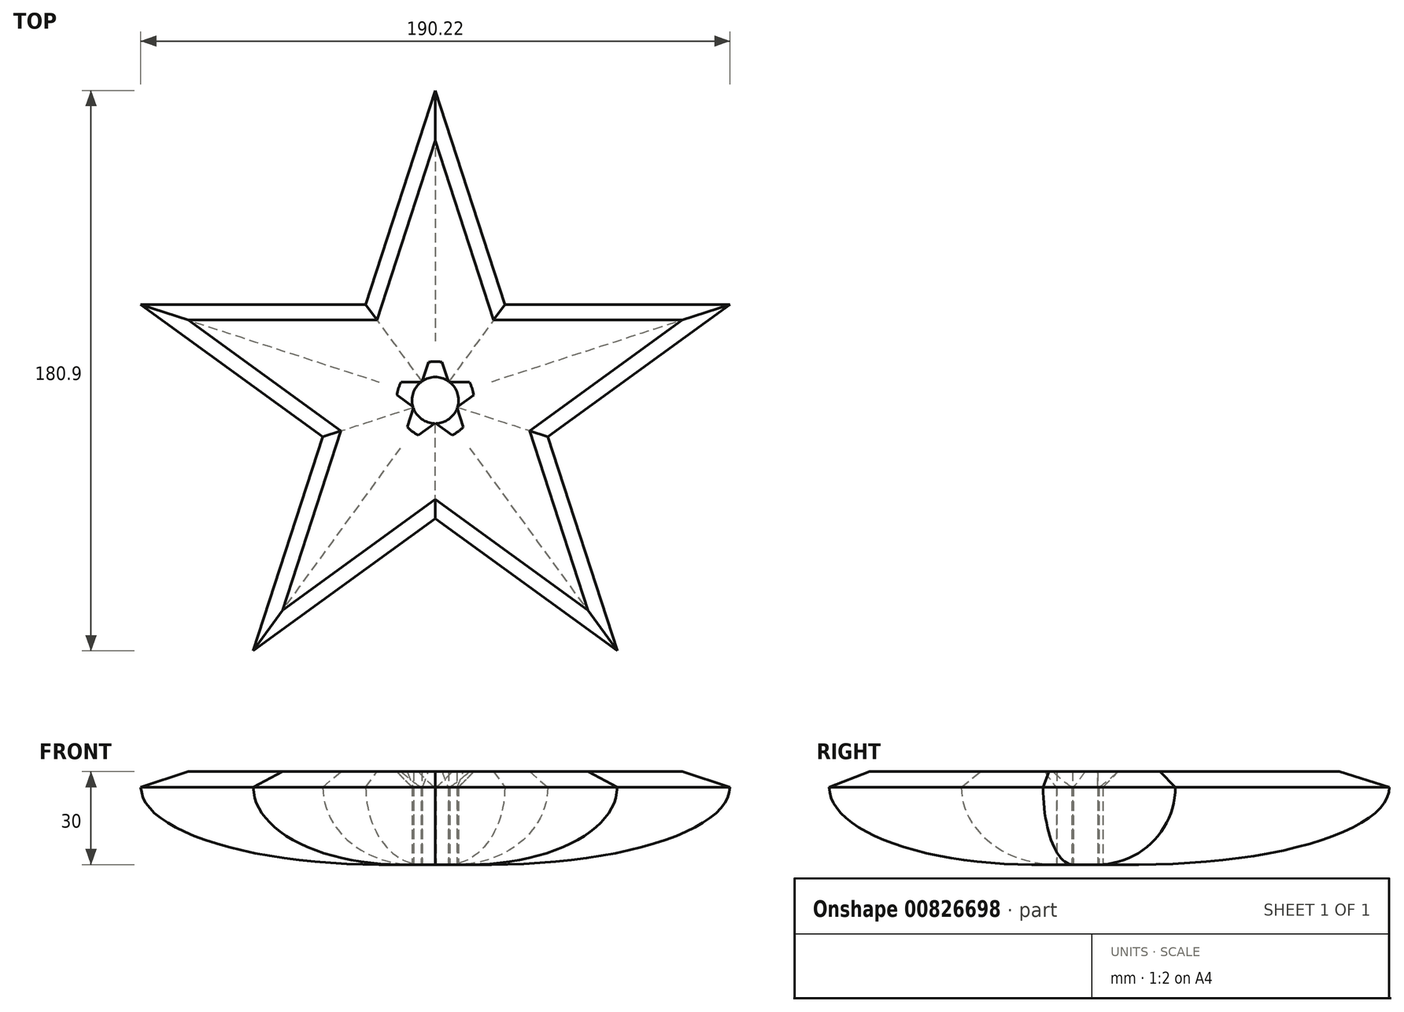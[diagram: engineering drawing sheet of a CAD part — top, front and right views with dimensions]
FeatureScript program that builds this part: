
annotation { "Feature Type Name" : "Feature", "Feature Type Description" : "" }
export const myFeature = defineFeature(function(context is Context, id is Id, definition is map)
    precondition{}
    {
        {
            var Q0;
            Q0=qCreatedBy(makeId("Top.planeOp"),FACE);
            var sketch = newSketch(context, id + "F0", { "sketchPlane" : qUnion([Q0])});
            skCircle(sketch, "E0.cCircle", {"center": v(0, 0) * mm, "radius": 100 * mm, "construction": true});
            skLineSegment(sketch, "E0.0", {"start": v(0, 100) * mm, "end": v(95.1, 30.9) * mm});
            skLineSegment(sketch, "E0.1", {"start": v(95.1, 30.9) * mm, "end": v(58.78, -80.9) * mm});
            skLineSegment(sketch, "E0.2", {"start": v(58.78, -80.9) * mm, "end": v(-58.78, -80.9) * mm});
            skLineSegment(sketch, "E0.3", {"start": v(-58.78, -80.9) * mm, "end": v(-95.1, 30.9) * mm});
            skLineSegment(sketch, "E0.4", {"start": v(-95.1, 30.9) * mm, "end": v(0, 100) * mm});
            skLineSegment(sketch, "E1", {"start": v(0, 100) * mm, "end": v(-22.45, 30.9) * mm});
            skLineSegment(sketch, "E2", {"start": v(95.1, 30.9) * mm, "end": v(22.45, 30.9) * mm});
            skLineSegment(sketch, "E3", {"start": v(-95.1, 30.9) * mm, "end": v(-36.33, -11.8) * mm});
            skLineSegment(sketch, "E4", {"start": v(0, 100) * mm, "end": v(22.45, 30.9) * mm});
            skLineSegment(sketch, "E5", {"start": v(-58.78, -80.9) * mm, "end": v(0, -38.2) * mm});
            skLineSegment(sketch, "E6.trimOffspring", {"start": v(-36.33, -11.8) * mm, "end": v(-58.78, -80.9) * mm});
            skLineSegment(sketch, "E7.trimOffspring", {"start": v(36.33, -11.8) * mm, "end": v(58.78, -80.9) * mm});
            skLineSegment(sketch, "E8.trimOffspring", {"start": v(-22.45, 30.9) * mm, "end": v(-95.1, 30.9) * mm});
            skLineSegment(sketch, "E9.trimOffspring", {"start": v(0, -38.2) * mm, "end": v(58.78, -80.9) * mm});
            skLineSegment(sketch, "E10.trimOffspring", {"start": v(36.33, -11.8) * mm, "end": v(95.1, 30.9) * mm});
            skSolve(sketch);
        }
        {
            var Q0;
            Q0=makeQuery(id+"F0.imprint","IMPRINT",FACE,{"disambiguationData":[TD([[makeQuery(id+"F0.imprint","IMPRINT",EDGE,{"derivedFrom":sQuery(id+"F0.wireOp",EDGE,"E1")}),1.0]])]});
            extrude(context, id + "F1", {"entities" : qUnion([Q0]), "depth" : 30 * mm, "offsetDistance" : 25 * mm});
        }
        {
            var Q0;
            Q0=makeQuery(id+"F1.opExtrude","CAP_FACE",FACE,{"disambiguationData":[OSD([sQuery(id+"F0.wireOp",EDGE,"E1"),sQuery(id+"F0.wireOp",EDGE,"E2"),sQuery(id+"F0.wireOp",EDGE,"E3"),sQuery(id+"F0.wireOp",EDGE,"E4"),sQuery(id+"F0.wireOp",EDGE,"E5"),sQuery(id+"F0.wireOp",EDGE,"E6.trimOffspring"),sQuery(id+"F0.wireOp",EDGE,"E7.trimOffspring"),sQuery(id+"F0.wireOp",EDGE,"E8.trimOffspring"),sQuery(id+"F0.wireOp",EDGE,"E9.trimOffspring"),sQuery(id+"F0.wireOp",EDGE,"E10.trimOffspring")])],"isStart":false});
            chamfer(context, id + "F2", {"entities" : qUnion([Q0]), "width" : 5 * mm, "tangentPropagation" : true});
        }
        {
            var Q0;
            Q0=makeQuery(id+"F1.opExtrude","CAP_FACE",FACE,{"disambiguationData":[OSD([sQuery(id+"F0.wireOp",EDGE,"E1"),sQuery(id+"F0.wireOp",EDGE,"E2"),sQuery(id+"F0.wireOp",EDGE,"E3"),sQuery(id+"F0.wireOp",EDGE,"E4"),sQuery(id+"F0.wireOp",EDGE,"E5"),sQuery(id+"F0.wireOp",EDGE,"E6.trimOffspring"),sQuery(id+"F0.wireOp",EDGE,"E7.trimOffspring"),sQuery(id+"F0.wireOp",EDGE,"E8.trimOffspring"),sQuery(id+"F0.wireOp",EDGE,"E9.trimOffspring"),sQuery(id+"F0.wireOp",EDGE,"E10.trimOffspring")])],"isStart":true});
            fillet(context, id + "F3", {"entities" : qUnion([Q0]), "radius" : 25 * mm, "tangentPropagation" : true, "allowEdgeOverflow" : false});
        }
        {
            var Q0;
            Q0=makeQuery(id+"F1.opExtrude","CAP_FACE",FACE,{"disambiguationData":[OSD([sQuery(id+"F0.wireOp",EDGE,"E1"),sQuery(id+"F0.wireOp",EDGE,"E2"),sQuery(id+"F0.wireOp",EDGE,"E3"),sQuery(id+"F0.wireOp",EDGE,"E4"),sQuery(id+"F0.wireOp",EDGE,"E5"),sQuery(id+"F0.wireOp",EDGE,"E6.trimOffspring"),sQuery(id+"F0.wireOp",EDGE,"E7.trimOffspring"),sQuery(id+"F0.wireOp",EDGE,"E8.trimOffspring"),sQuery(id+"F0.wireOp",EDGE,"E9.trimOffspring"),sQuery(id+"F0.wireOp",EDGE,"E10.trimOffspring")])],"isStart":true});
            var sketch = newSketch(context, id + "F4", { "sketchPlane" : qUnion([Q0])});
            skCircle(sketch, "E11", {"center": v(0, 0) * mm, "radius": 7.5 * mm});
            skSolve(sketch);
        }
        {
            var Q0;
            {var subQ0=sQuery(id+"F0.wireOp",EDGE,"E10.trimOffspring");var subQ1=sQuery(id+"F0.wireOp",EDGE,"E9.trimOffspring");var subQ2=sQuery(id+"F0.wireOp",EDGE,"E8.trimOffspring");var subQ3=sQuery(id+"F0.wireOp",EDGE,"E7.trimOffspring");var subQ4=sQuery(id+"F0.wireOp",EDGE,"E6.trimOffspring");var subQ5=sQuery(id+"F0.wireOp",EDGE,"E5");var subQ6=sQuery(id+"F0.wireOp",EDGE,"E4");var subQ7=sQuery(id+"F0.wireOp",EDGE,"E3");var subQ8=sQuery(id+"F0.wireOp",EDGE,"E2");var subQ9=sQuery(id+"F0.wireOp",EDGE,"E1");var subQ10=makeQuery(id+"F1.opExtrude","CAP_FACE",FACE,{"disambiguationData":[OSD([subQ9,subQ8,subQ7,subQ6,subQ5,subQ4,subQ3,subQ2,subQ1,subQ0])],"isStart":true});var subQ14=sQuery(id+"F4.wireOp",EDGE,"E11");var subQ31=makeQuery(id+"F3.opFillet","BLEND_EDGE",EDGE,{"blendedFrom":[makeQuery(id+"F1.opExtrude","CAP_EDGE",EDGE,{"disambiguationData":[OSD([subQ3])],"isStart":true}),subQ10],"blendedInto":[subQ10]});var subQ32=makeQuery(id+"F4.imprint","INTERSECT",VERTEX,{"derivedFrom":[subQ31,subQ14]});Q0=makeQuery(id+"F4.imprint","IMPRINT",FACE,{"disambiguationData":[TD([[makeQuery(id+"F4.imprint","IMPRINT",EDGE,{"disambiguationData":[TD([[subQ32,-1.0]])],"derivedFrom":subQ14}),1.0]])]});}
            extrude(context, id + "F5", {"entities" : qUnion([Q0]), "operationType" : NewBodyOperationType.REMOVE, "oppositeDirection" : true, "depth" : 35 * mm, "offsetDistance" : 25 * mm});
        }
        {
            var Q0;
            {var subQ0=sQuery(id+"F4.wireOp",EDGE,"E11");var subQ1=sQuery(id+"F0.wireOp",EDGE,"E10.trimOffspring");var subQ2=sQuery(id+"F0.wireOp",EDGE,"E9.trimOffspring");var subQ3=sQuery(id+"F0.wireOp",EDGE,"E8.trimOffspring");var subQ4=sQuery(id+"F0.wireOp",EDGE,"E7.trimOffspring");var subQ5=sQuery(id+"F0.wireOp",EDGE,"E6.trimOffspring");var subQ6=sQuery(id+"F0.wireOp",EDGE,"E5");var subQ7=sQuery(id+"F0.wireOp",EDGE,"E4");var subQ8=sQuery(id+"F0.wireOp",EDGE,"E3");var subQ9=sQuery(id+"F0.wireOp",EDGE,"E2");var subQ10=sQuery(id+"F0.wireOp",EDGE,"E1");var subQ11=makeQuery(id+"F1.opExtrude","CAP_FACE",FACE,{"disambiguationData":[OSD([subQ10,subQ9,subQ8,subQ7,subQ6,subQ5,subQ4,subQ3,subQ2,subQ1])],"isStart":true});Q0=makeQuery(id+"F5.boolean.opBoolean","INTERSECT",EDGE,{"derivedFrom":[makeQuery(id+"F1.opExtrude","CAP_FACE",FACE,{"disambiguationData":[OSD([subQ10,subQ9,subQ8,subQ7,subQ6,subQ5,subQ4,subQ3,subQ2,subQ1])],"isStart":false}),makeQuery(id+"F5.opExtrude","SWEPT_FACE",FACE,{"disambiguationData":[OSD([subQ0]),TDD([makeQuery(id+"F4.imprint","IMPRINT",EDGE,{"disambiguationData":[TD([[makeQuery(id+"F4.imprint","INTERSECT",VERTEX,{"derivedFrom":[makeQuery(id+"F3.opFillet","BLEND_EDGE",EDGE,{"blendedFrom":[makeQuery(id+"F1.opExtrude","CAP_EDGE",EDGE,{"disambiguationData":[OSD([subQ8])],"isStart":true}),subQ11],"blendedInto":[subQ11]}),subQ0]}),-1.0]])],"derivedFrom":subQ0})])]})]});}
            var Q1;
            {var subQ0=sQuery(id+"F4.wireOp",EDGE,"E11");var subQ1=sQuery(id+"F0.wireOp",EDGE,"E10.trimOffspring");var subQ2=sQuery(id+"F0.wireOp",EDGE,"E9.trimOffspring");var subQ3=sQuery(id+"F0.wireOp",EDGE,"E8.trimOffspring");var subQ4=sQuery(id+"F0.wireOp",EDGE,"E7.trimOffspring");var subQ5=sQuery(id+"F0.wireOp",EDGE,"E6.trimOffspring");var subQ6=sQuery(id+"F0.wireOp",EDGE,"E5");var subQ7=sQuery(id+"F0.wireOp",EDGE,"E4");var subQ8=sQuery(id+"F0.wireOp",EDGE,"E3");var subQ9=sQuery(id+"F0.wireOp",EDGE,"E2");var subQ10=sQuery(id+"F0.wireOp",EDGE,"E1");var subQ11=makeQuery(id+"F1.opExtrude","CAP_FACE",FACE,{"disambiguationData":[OSD([subQ10,subQ9,subQ8,subQ7,subQ6,subQ5,subQ4,subQ3,subQ2,subQ1])],"isStart":true});Q1=makeQuery(id+"F5.boolean.opBoolean","INTERSECT",EDGE,{"derivedFrom":[makeQuery(id+"F1.opExtrude","CAP_FACE",FACE,{"disambiguationData":[OSD([subQ10,subQ9,subQ8,subQ7,subQ6,subQ5,subQ4,subQ3,subQ2,subQ1])],"isStart":false}),makeQuery(id+"F5.opExtrude","SWEPT_FACE",FACE,{"disambiguationData":[OSD([subQ0]),TDD([makeQuery(id+"F4.imprint","IMPRINT",EDGE,{"disambiguationData":[TD([[makeQuery(id+"F4.imprint","INTERSECT",VERTEX,{"derivedFrom":[makeQuery(id+"F3.opFillet","BLEND_EDGE",EDGE,{"blendedFrom":[makeQuery(id+"F1.opExtrude","CAP_EDGE",EDGE,{"disambiguationData":[OSD([subQ10])],"isStart":true}),subQ11],"blendedInto":[subQ11]}),subQ0]}),-1.0]])],"derivedFrom":subQ0})])]})]});}
            var Q2;
            {var subQ0=sQuery(id+"F4.wireOp",EDGE,"E11");var subQ1=sQuery(id+"F0.wireOp",EDGE,"E10.trimOffspring");var subQ2=sQuery(id+"F0.wireOp",EDGE,"E9.trimOffspring");var subQ3=sQuery(id+"F0.wireOp",EDGE,"E8.trimOffspring");var subQ4=sQuery(id+"F0.wireOp",EDGE,"E7.trimOffspring");var subQ5=sQuery(id+"F0.wireOp",EDGE,"E6.trimOffspring");var subQ6=sQuery(id+"F0.wireOp",EDGE,"E5");var subQ7=sQuery(id+"F0.wireOp",EDGE,"E4");var subQ8=sQuery(id+"F0.wireOp",EDGE,"E3");var subQ9=sQuery(id+"F0.wireOp",EDGE,"E2");var subQ10=sQuery(id+"F0.wireOp",EDGE,"E1");var subQ11=makeQuery(id+"F1.opExtrude","CAP_FACE",FACE,{"disambiguationData":[OSD([subQ10,subQ9,subQ8,subQ7,subQ6,subQ5,subQ4,subQ3,subQ2,subQ1])],"isStart":true});Q2=makeQuery(id+"F5.boolean.opBoolean","INTERSECT",EDGE,{"derivedFrom":[makeQuery(id+"F1.opExtrude","CAP_FACE",FACE,{"disambiguationData":[OSD([subQ10,subQ9,subQ8,subQ7,subQ6,subQ5,subQ4,subQ3,subQ2,subQ1])],"isStart":false}),makeQuery(id+"F5.opExtrude","SWEPT_FACE",FACE,{"disambiguationData":[OSD([subQ0]),TDD([makeQuery(id+"F4.imprint","IMPRINT",EDGE,{"disambiguationData":[TD([[makeQuery(id+"F4.imprint","INTERSECT",VERTEX,{"derivedFrom":[makeQuery(id+"F3.opFillet","BLEND_EDGE",EDGE,{"blendedFrom":[makeQuery(id+"F1.opExtrude","CAP_EDGE",EDGE,{"disambiguationData":[OSD([subQ1])],"isStart":true}),subQ11],"blendedInto":[subQ11]}),subQ0]}),1.0]])],"derivedFrom":subQ0})])]})]});}
            var Q3;
            {var subQ0=sQuery(id+"F4.wireOp",EDGE,"E11");var subQ1=sQuery(id+"F0.wireOp",EDGE,"E10.trimOffspring");var subQ2=sQuery(id+"F0.wireOp",EDGE,"E9.trimOffspring");var subQ3=sQuery(id+"F0.wireOp",EDGE,"E8.trimOffspring");var subQ4=sQuery(id+"F0.wireOp",EDGE,"E7.trimOffspring");var subQ5=sQuery(id+"F0.wireOp",EDGE,"E6.trimOffspring");var subQ6=sQuery(id+"F0.wireOp",EDGE,"E5");var subQ7=sQuery(id+"F0.wireOp",EDGE,"E4");var subQ8=sQuery(id+"F0.wireOp",EDGE,"E3");var subQ9=sQuery(id+"F0.wireOp",EDGE,"E2");var subQ10=sQuery(id+"F0.wireOp",EDGE,"E1");var subQ11=makeQuery(id+"F1.opExtrude","CAP_FACE",FACE,{"disambiguationData":[OSD([subQ10,subQ9,subQ8,subQ7,subQ6,subQ5,subQ4,subQ3,subQ2,subQ1])],"isStart":true});Q3=makeQuery(id+"F5.boolean.opBoolean","INTERSECT",EDGE,{"derivedFrom":[makeQuery(id+"F1.opExtrude","CAP_FACE",FACE,{"disambiguationData":[OSD([subQ10,subQ9,subQ8,subQ7,subQ6,subQ5,subQ4,subQ3,subQ2,subQ1])],"isStart":false}),makeQuery(id+"F5.opExtrude","SWEPT_FACE",FACE,{"disambiguationData":[OSD([subQ0]),TDD([makeQuery(id+"F4.imprint","IMPRINT",EDGE,{"disambiguationData":[TD([[makeQuery(id+"F4.imprint","INTERSECT",VERTEX,{"derivedFrom":[makeQuery(id+"F3.opFillet","BLEND_EDGE",EDGE,{"blendedFrom":[makeQuery(id+"F1.opExtrude","CAP_EDGE",EDGE,{"disambiguationData":[OSD([subQ4])],"isStart":true}),subQ11],"blendedInto":[subQ11]}),subQ0]}),-1.0]])],"derivedFrom":subQ0})])]})]});}
            var Q4;
            {var subQ0=sQuery(id+"F4.wireOp",EDGE,"E11");var subQ1=sQuery(id+"F0.wireOp",EDGE,"E10.trimOffspring");var subQ2=sQuery(id+"F0.wireOp",EDGE,"E9.trimOffspring");var subQ3=sQuery(id+"F0.wireOp",EDGE,"E8.trimOffspring");var subQ4=sQuery(id+"F0.wireOp",EDGE,"E7.trimOffspring");var subQ5=sQuery(id+"F0.wireOp",EDGE,"E6.trimOffspring");var subQ6=sQuery(id+"F0.wireOp",EDGE,"E5");var subQ7=sQuery(id+"F0.wireOp",EDGE,"E4");var subQ8=sQuery(id+"F0.wireOp",EDGE,"E3");var subQ9=sQuery(id+"F0.wireOp",EDGE,"E2");var subQ10=sQuery(id+"F0.wireOp",EDGE,"E1");var subQ11=makeQuery(id+"F1.opExtrude","CAP_FACE",FACE,{"disambiguationData":[OSD([subQ10,subQ9,subQ8,subQ7,subQ6,subQ5,subQ4,subQ3,subQ2,subQ1])],"isStart":true});Q4=makeQuery(id+"F5.boolean.opBoolean","INTERSECT",EDGE,{"derivedFrom":[makeQuery(id+"F1.opExtrude","CAP_FACE",FACE,{"disambiguationData":[OSD([subQ10,subQ9,subQ8,subQ7,subQ6,subQ5,subQ4,subQ3,subQ2,subQ1])],"isStart":false}),makeQuery(id+"F5.opExtrude","SWEPT_FACE",FACE,{"disambiguationData":[OSD([subQ0]),TDD([makeQuery(id+"F4.imprint","IMPRINT",EDGE,{"disambiguationData":[TD([[makeQuery(id+"F4.imprint","INTERSECT",VERTEX,{"derivedFrom":[makeQuery(id+"F3.opFillet","BLEND_EDGE",EDGE,{"blendedFrom":[makeQuery(id+"F1.opExtrude","CAP_EDGE",EDGE,{"disambiguationData":[OSD([subQ6])],"isStart":true}),subQ11],"blendedInto":[subQ11]}),subQ0]}),-1.0]])],"derivedFrom":subQ0})])]})]});}
            chamfer(context, id + "F6", {"entities" : qUnion([Q0, Q1, Q2, Q3, Q4]), "width" : 5 * mm, "tangentPropagation" : true});
        }
    });
